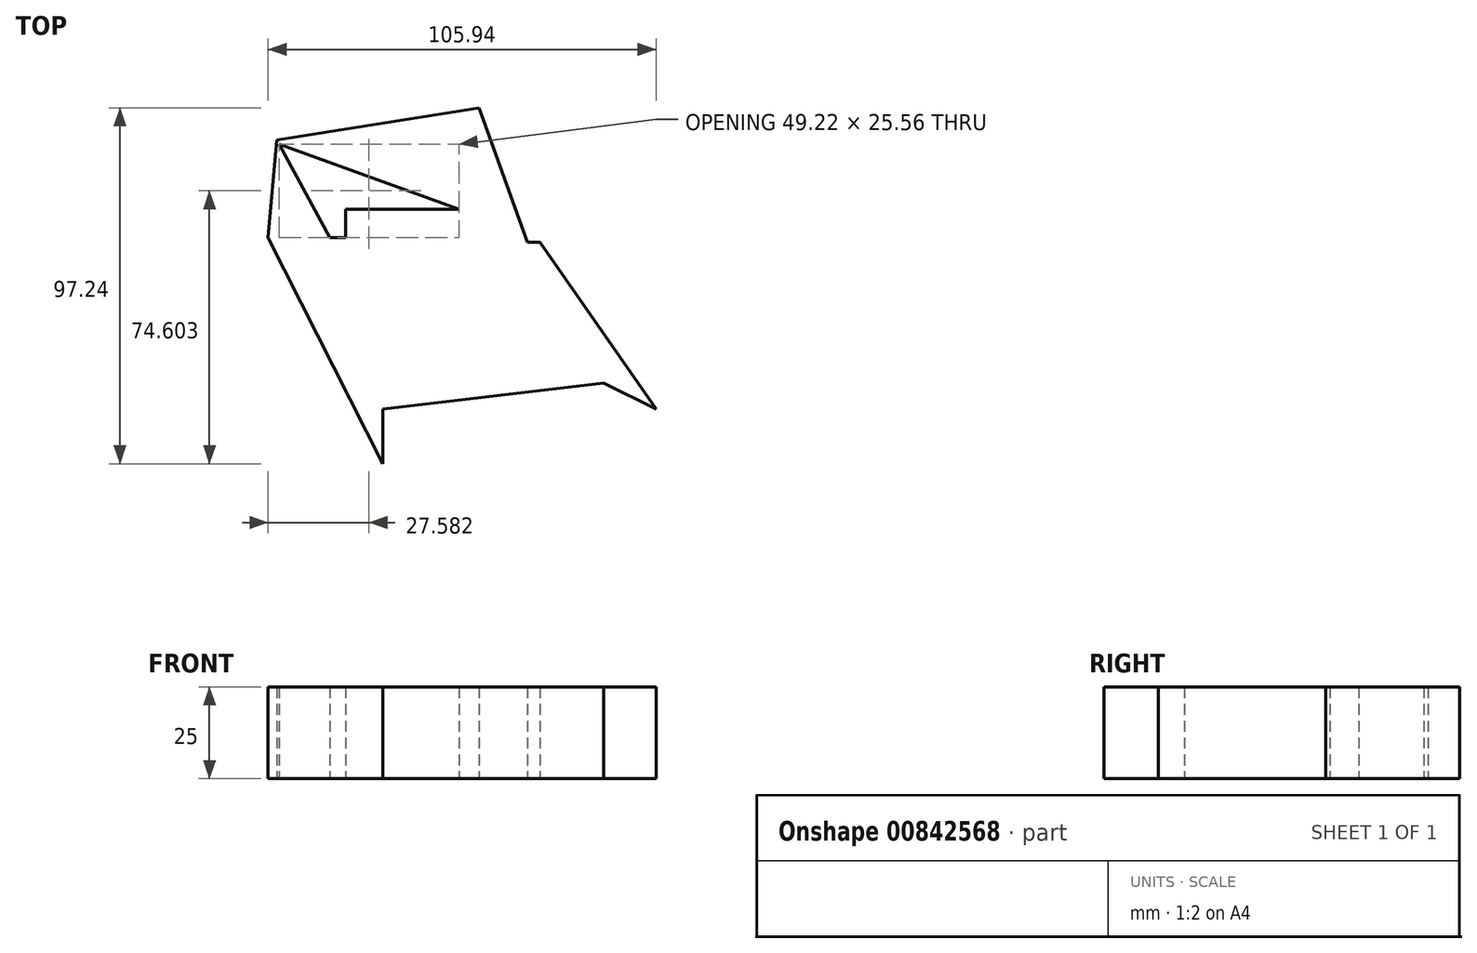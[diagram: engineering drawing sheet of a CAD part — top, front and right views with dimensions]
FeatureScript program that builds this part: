
annotation { "Feature Type Name" : "Feature", "Feature Type Description" : "" }
export const myFeature = defineFeature(function(context is Context, id is Id, definition is map)
    precondition{}
    {
        {
            var Q0;
            Q0=qCreatedBy(makeId("Top.planeOp"),FACE);
            var sketch = newSketch(context, id + "F0", { "sketchPlane" : qUnion([Q0])});
            skLineSegment(sketch, "E0", {"start": v(-43.34, 29.2) * mm, "end": v(-22.21, 29.2) * mm});
            skLineSegment(sketch, "E1", {"start": v(-22.21, 29.2) * mm, "end": v(-22.21, 36.97) * mm});
            skLineSegment(sketch, "E2", {"start": v(-22.21, 36.97) * mm, "end": v(8.85, 36.97) * mm});
            skLineSegment(sketch, "E3", {"start": v(8.85, 36.97) * mm, "end": v(8.85, 27.96) * mm});
            skLineSegment(sketch, "E4", {"start": v(8.85, 27.96) * mm, "end": v(30.9, 27.96) * mm});
            skLineSegment(sketch, "E5", {"start": v(30.9, 27.96) * mm, "end": v(62.6, -17.7) * mm});
            skLineSegment(sketch, "E6", {"start": v(-43.34, 29.2) * mm, "end": v(-11.96, -32.62) * mm});
            skLineSegment(sketch, "E7", {"start": v(-11.96, -32.62) * mm, "end": v(-11.96, -17.7) * mm});
            skLineSegment(sketch, "E8", {"start": v(-11.96, -17.7) * mm, "end": v(48.3, -10.56) * mm});
            skLineSegment(sketch, "E9", {"start": v(48.3, -10.56) * mm, "end": v(62.6, -17.7) * mm});
            skLineSegment(sketch, "E10", {"start": v(156.72, 29.2) * mm, "end": v(147.71, 24.6) * mm});
            skLineSegment(sketch, "E11", {"start": v(-11.96, -17.7) * mm, "end": v(-15.01, 8.05) * mm});
            skLineSegment(sketch, "E12", {"start": v(-15.01, 8.05) * mm, "end": v(31.39, 17.09) * mm});
            skLineSegment(sketch, "E13", {"start": v(31.39, 17.09) * mm, "end": v(48.3, -10.56) * mm});
            skLineSegment(sketch, "E14", {"start": v(-43.34, 29.2) * mm, "end": v(-41, 55.92) * mm});
            skLineSegment(sketch, "E15", {"start": v(-41, 55.92) * mm, "end": v(-15.01, 8.05) * mm});
            skLineSegment(sketch, "E16", {"start": v(31.39, 17.09) * mm, "end": v(14.3, 64.62) * mm});
            skLineSegment(sketch, "E17", {"start": v(14.3, 64.62) * mm, "end": v(-41, 55.92) * mm});
            skLineSegment(sketch, "E18", {"start": v(-22.21, 36.97) * mm, "end": v(-40.37, 54.77) * mm});
            skLineSegment(sketch, "E19", {"start": v(-40.37, 54.77) * mm, "end": v(8.85, 36.97) * mm});
            skLineSegment(sketch, "E20", {"start": v(14.3, 64.62) * mm, "end": v(8.85, 36.97) * mm});
            skSolve(sketch);
        }
        {
            var Q0;
            Q0 = qSketchRegion(id + "F0", true);
            extrude(context, id + "F1", {"entities" : qUnion([Q0]), "depth" : 25 * mm, "offsetDistance" : 25 * mm});
        }
    });
